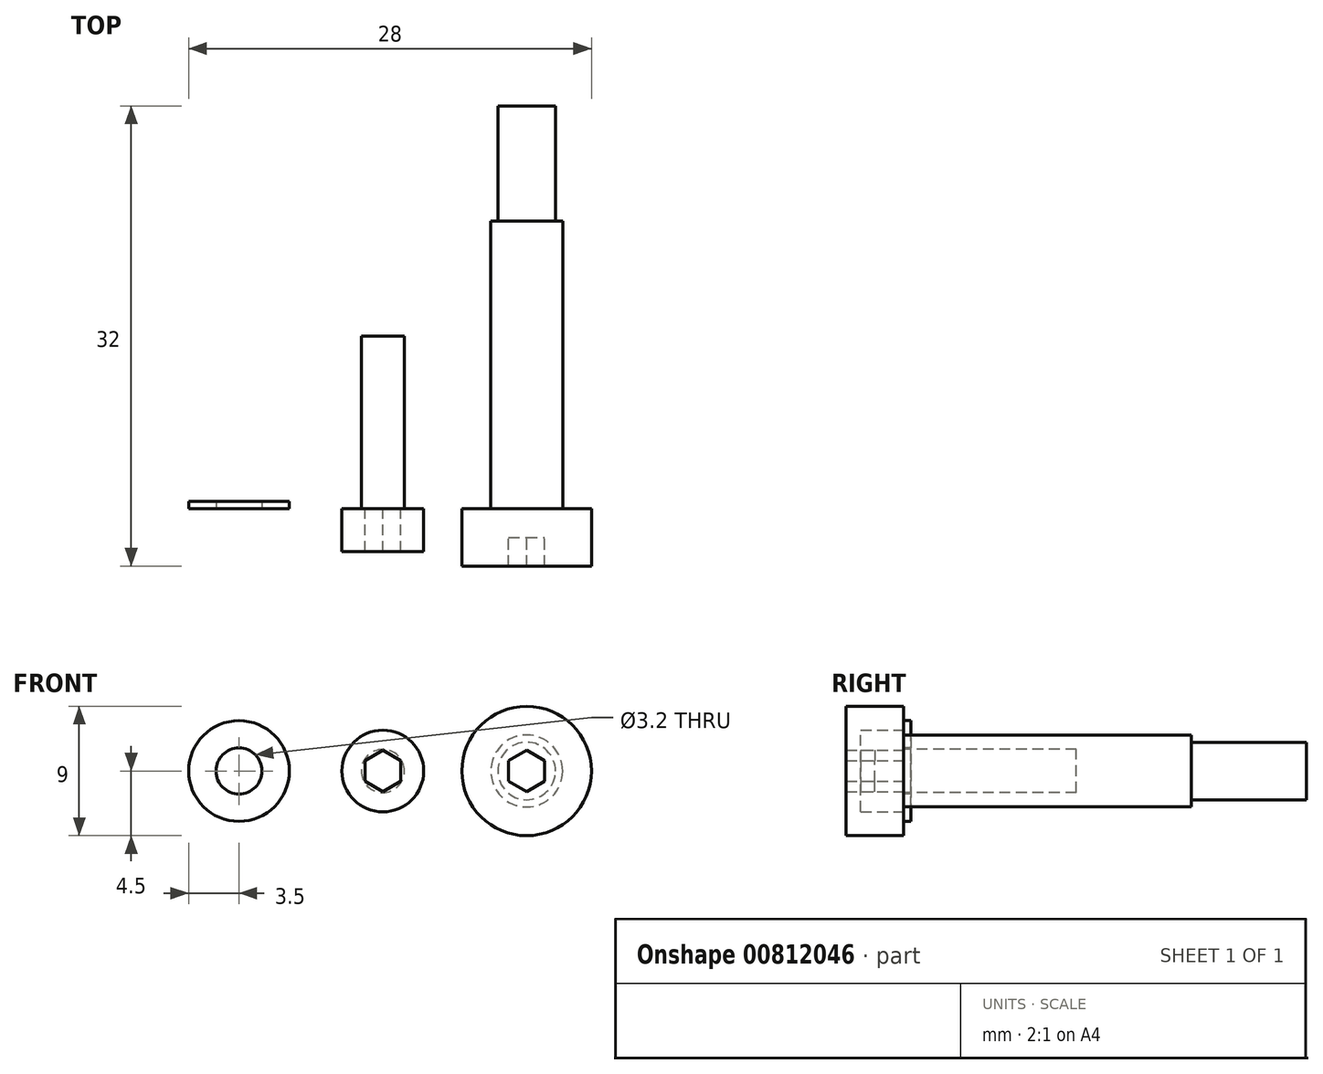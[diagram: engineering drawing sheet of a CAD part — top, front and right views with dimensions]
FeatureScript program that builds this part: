
annotation { "Feature Type Name" : "Feature", "Feature Type Description" : "" }
export const myFeature = defineFeature(function(context is Context, id is Id, definition is map)
    precondition{}
    {
        {
            var Q0;
            Q0=qCreatedBy(makeId("Front.planeOp"),FACE);
            var sketch = newSketch(context, id + "F0", { "sketchPlane" : qUnion([Q0])});
            skCircle(sketch, "E0", {"center": v(0, 0) * mm, "radius": 2.84 * mm});
            skCircle(sketch, "E1", {"center": v(0, 0) * mm, "radius": 1.5 * mm});
            skCircle(sketch, "E2.cCircle", {"center": v(0, 0) * mm, "radius": 1.25 * mm, "construction": true});
            skLineSegment(sketch, "E2.0", {"start": v(1.25, 0.72) * mm, "end": v(1.25, -0.72) * mm});
            skLineSegment(sketch, "E2.1", {"start": v(1.25, -0.72) * mm, "end": v(0, -1.44) * mm});
            skLineSegment(sketch, "E2.2", {"start": v(0, -1.44) * mm, "end": v(-1.25, -0.72) * mm});
            skLineSegment(sketch, "E2.3", {"start": v(-1.25, -0.72) * mm, "end": v(-1.25, 0.72) * mm});
            skLineSegment(sketch, "E2.4", {"start": v(-1.25, 0.72) * mm, "end": v(0, 1.44) * mm});
            skLineSegment(sketch, "E2.5", {"start": v(0, 1.44) * mm, "end": v(1.25, 0.72) * mm});
            skPoint(sketch, "E2.0.midPoint", {"position": v(1.25, 0) * mm});
            skSolve(sketch);
        }
        {
            var Q0;
            Q0=makeQuery(id+"F0.imprint","IMPRINT",FACE,{"disambiguationData":[TD([[makeQuery(id+"F0.imprint","IMPRINT",EDGE,{"derivedFrom":sQuery(id+"F0.wireOp",EDGE,"E1")}),1.0]])]});
            var Q1;
            Q1=makeQuery(id+"F0.imprint","IMPRINT",FACE,{"disambiguationData":[TD([[makeQuery(id+"F0.imprint","IMPRINT",EDGE,{"derivedFrom":sQuery(id+"F0.wireOp",EDGE,"E2.0")}),-1.0]])]});
            extrude(context, id + "F1", {"entities" : qUnion([Q0, Q1]), "oppositeDirection" : true, "depth" : 12 * mm, "offsetDistance" : 25 * mm});
        }
        {
            var Q0;
            Q0=makeQuery(id+"F0.imprint","IMPRINT",FACE,{"disambiguationData":[TD([[makeQuery(id+"F0.imprint","IMPRINT",EDGE,{"derivedFrom":sQuery(id+"F0.wireOp",EDGE,"E0")}),1.0]])]});
            var Q1;
            Q1=makeQuery(id+"F0.imprint","IMPRINT",FACE,{"disambiguationData":[TD([[makeQuery(id+"F0.imprint","IMPRINT",EDGE,{"derivedFrom":sQuery(id+"F0.wireOp",EDGE,"E1")}),-1.0]])]});
            var Q2;
            Q2=makeQuery(id+"F0.imprint","IMPRINT",FACE,{"disambiguationData":[TD([[makeQuery(id+"F0.imprint","IMPRINT",EDGE,{"derivedFrom":sQuery(id+"F0.wireOp",EDGE,"E1")}),1.0]])]});
            extrude(context, id + "F2", {"entities" : qUnion([Q0, Q1, Q2]), "operationType" : NewBodyOperationType.ADD, "depth" : 3 * mm, "offsetDistance" : 25 * mm});
        }
        {
            var Q0;
            Q0=makeQuery(id+"F0.imprint","IMPRINT",FACE,{"disambiguationData":[TD([[makeQuery(id+"F0.imprint","IMPRINT",EDGE,{"derivedFrom":sQuery(id+"F0.wireOp",EDGE,"E2.0")}),-1.0]])]});
            extrude(context, id + "F3", {"entities" : qUnion([Q0]), "operationType" : NewBodyOperationType.REMOVE, "depth" : 25 * mm, "offsetDistance" : 25 * mm, "hasSecondDirection" : true, "secondDirectionOppositeDirection" : false, "secondDirectionDepth" : 1.9 * mm});
        }
        {
            var Q0;
            Q0=qCreatedBy(makeId("Front.planeOp"),FACE);
            var sketch = newSketch(context, id + "F4", { "sketchPlane" : qUnion([Q0])});
            skCircle(sketch, "E3", {"center": v(10, 0) * mm, "radius": 4.5 * mm});
            skCircle(sketch, "E4", {"center": v(10, 0) * mm, "radius": 2.5 * mm});
            skCircle(sketch, "E5", {"center": v(10, 0) * mm, "radius": 2 * mm});
            skCircle(sketch, "E6.cCircle", {"center": v(10, 0) * mm, "radius": 1.25 * mm, "construction": true});
            skLineSegment(sketch, "E6.0", {"start": v(11.25, 0.72) * mm, "end": v(11.25, -0.72) * mm});
            skLineSegment(sketch, "E6.1", {"start": v(11.25, -0.72) * mm, "end": v(10, -1.44) * mm});
            skLineSegment(sketch, "E6.2", {"start": v(10, -1.44) * mm, "end": v(8.75, -0.72) * mm});
            skLineSegment(sketch, "E6.3", {"start": v(8.75, -0.72) * mm, "end": v(8.75, 0.72) * mm});
            skLineSegment(sketch, "E6.4", {"start": v(8.75, 0.72) * mm, "end": v(10, 1.44) * mm});
            skLineSegment(sketch, "E6.5", {"start": v(10, 1.44) * mm, "end": v(11.25, 0.72) * mm});
            skPoint(sketch, "E6.0.midPoint", {"position": v(11.25, 0) * mm});
            skSolve(sketch);
        }
        {
            var Q0;
            Q0=makeQuery(id+"F4.imprint","IMPRINT",FACE,{"disambiguationData":[TD([[makeQuery(id+"F4.imprint","IMPRINT",EDGE,{"derivedFrom":sQuery(id+"F4.wireOp",EDGE,"E3")}),1.0]])]});
            var Q1;
            Q1=makeQuery(id+"F4.imprint","IMPRINT",FACE,{"disambiguationData":[TD([[makeQuery(id+"F4.imprint","IMPRINT",EDGE,{"derivedFrom":sQuery(id+"F4.wireOp",EDGE,"E4")}),1.0]])]});
            var Q2;
            Q2=makeQuery(id+"F4.imprint","IMPRINT",FACE,{"disambiguationData":[TD([[makeQuery(id+"F4.imprint","IMPRINT",EDGE,{"derivedFrom":sQuery(id+"F4.wireOp",EDGE,"E5")}),1.0]])]});
            var Q3;
            Q3=makeQuery(id+"F4.imprint","IMPRINT",FACE,{"disambiguationData":[TD([[makeQuery(id+"F4.imprint","IMPRINT",EDGE,{"derivedFrom":sQuery(id+"F4.wireOp",EDGE,"E6.0")}),-1.0]])]});
            extrude(context, id + "F5", {"entities" : qUnion([Q0, Q1, Q2, Q3]), "depth" : 4 * mm, "offsetDistance" : 25 * mm});
        }
        {
            var Q0;
            Q0=makeQuery(id+"F4.imprint","IMPRINT",FACE,{"disambiguationData":[TD([[makeQuery(id+"F4.imprint","IMPRINT",EDGE,{"derivedFrom":sQuery(id+"F4.wireOp",EDGE,"E4")}),1.0]])]});
            var Q1;
            Q1=makeQuery(id+"F4.imprint","IMPRINT",FACE,{"disambiguationData":[TD([[makeQuery(id+"F4.imprint","IMPRINT",EDGE,{"derivedFrom":sQuery(id+"F4.wireOp",EDGE,"E5")}),1.0]])]});
            var Q2;
            Q2=makeQuery(id+"F4.imprint","IMPRINT",FACE,{"disambiguationData":[TD([[makeQuery(id+"F4.imprint","IMPRINT",EDGE,{"derivedFrom":sQuery(id+"F4.wireOp",EDGE,"E6.0")}),-1.0]])]});
            extrude(context, id + "F6", {"entities" : qUnion([Q0, Q1, Q2]), "operationType" : NewBodyOperationType.ADD, "oppositeDirection" : true, "depth" : 20 * mm, "offsetDistance" : 25 * mm});
        }
        {
            var Q0;
            Q0=makeQuery(id+"F4.imprint","IMPRINT",FACE,{"disambiguationData":[TD([[makeQuery(id+"F4.imprint","IMPRINT",EDGE,{"derivedFrom":sQuery(id+"F4.wireOp",EDGE,"E5")}),1.0]])]});
            var Q1;
            Q1=makeQuery(id+"F4.imprint","IMPRINT",FACE,{"disambiguationData":[TD([[makeQuery(id+"F4.imprint","IMPRINT",EDGE,{"derivedFrom":sQuery(id+"F4.wireOp",EDGE,"E6.0")}),-1.0]])]});
            var Q2;
            Q2=sQuery(id+"F4.wireOp",EDGE,"E5");
            extrude(context, id + "F7", {"entities" : qUnion([Q0, Q1]), "operationType" : NewBodyOperationType.ADD, "surfaceEntities" : qUnion([Q2]), "oppositeDirection" : true, "depth" : (20 + 8) * mm, "offsetDistance" : 25 * mm});
        }
        {
            var Q0;
            Q0=qCreatedBy(makeId("Front.planeOp"),FACE);
            var sketch = newSketch(context, id + "F8", { "sketchPlane" : qUnion([Q0])});
            skCircle(sketch, "E7", {"center": v(-10, 0) * mm, "radius": 3.5 * mm});
            skCircle(sketch, "E8", {"center": v(-10, 0) * mm, "radius": 1.6 * mm});
            skSolve(sketch);
        }
        {
            var Q0;
            Q0=makeQuery(id+"F8.imprint","IMPRINT",FACE,{"disambiguationData":[TD([[makeQuery(id+"F8.imprint","IMPRINT",EDGE,{"derivedFrom":sQuery(id+"F8.wireOp",EDGE,"E7")}),1.0]])]});
            extrude(context, id + "F9", {"entities" : qUnion([Q0]), "oppositeDirection" : true, "depth" : 0.5 * mm, "offsetDistance" : 25 * mm});
        }
        {
            var Q0;
            Q0=makeQuery(id+"F4.imprint","IMPRINT",FACE,{"disambiguationData":[TD([[makeQuery(id+"F4.imprint","IMPRINT",EDGE,{"derivedFrom":sQuery(id+"F4.wireOp",EDGE,"E6.0")}),-1.0]])]});
            extrude(context, id + "F10", {"entities" : qUnion([Q0]), "operationType" : NewBodyOperationType.REMOVE, "endBound" : BoundingType.UP_TO_NEXT, "depth" : 25 * mm, "offsetDistance" : 25 * mm, "hasSecondDirection" : true, "secondDirectionOppositeDirection" : false, "secondDirectionDepth" : 2 * mm});
        }
    });
